# Revit family: 654_79bbd8845d444c6198e4e6afc458d6
name_source: partatom
category: Data Devices
revit_build: Autodesk Revit 2018 (Build: 20170223_1515(x64)
units: mm (PartAtom-declared; Revit-internal decimal feet)

## family parameters
Always vertical = Yes
Cut with Voids When Loaded = No
Maintain Annotation Orientation = Yes
Part Type = Normal
Room Calculation Point = No
Round Connector Dimension = Use Diameter
Shared = No
Work Plane-Based = No

## types (1)
- 110987
    Description = Humidity sensor
    L2D = 0 mm  [stored 0 ft]
    MC Active Power = 0 W
    MC CosPhi = 0.95
    MC Number of Poles = 1
    MC Product Code = 110987
    MC Voltage = 230 V
    Manufacturer = Flexit
    URL = www.flexit.no
    W2D = 0 mm  [stored 0 ft]
    X1 = 35 mm
    X2 = 1 mm  [stored 0.00328084 ft]
    X3 = 43 mm  [stored 0.141076 ft]
    X4 = 39 mm
    Y0 = 5 mm  [stored 0.0164042 ft]
    Y1 = 6 mm  [stored 0.019685 ft]
    Y2 = 9 mm  [stored 0.0295276 ft]
    Y3 = 1 mm  [stored 0.00328084 ft]
    Z1 = 35 mm
    Z2 = 1 mm  [stored 0.00328084 ft]
    Z3 = 43 mm  [stored 0.141076 ft]
    Z4 = 39 mm
    magiApparentLoad = 0 VA
    magiPartTypeId = 654
    magiProductFamilyId = 79bbd8845d444c6198e4e6afc458d6
    magiProductId = b0175a20089e4cd3868578ba6818c8

note: [stored X ft] marks values corroborated as IEEE doubles in the binary element streams (Revit-internal decimal feet)

## geometry (parser evidence)
native form markers: Sweep x2
no freeform markers — native parametric forms only
